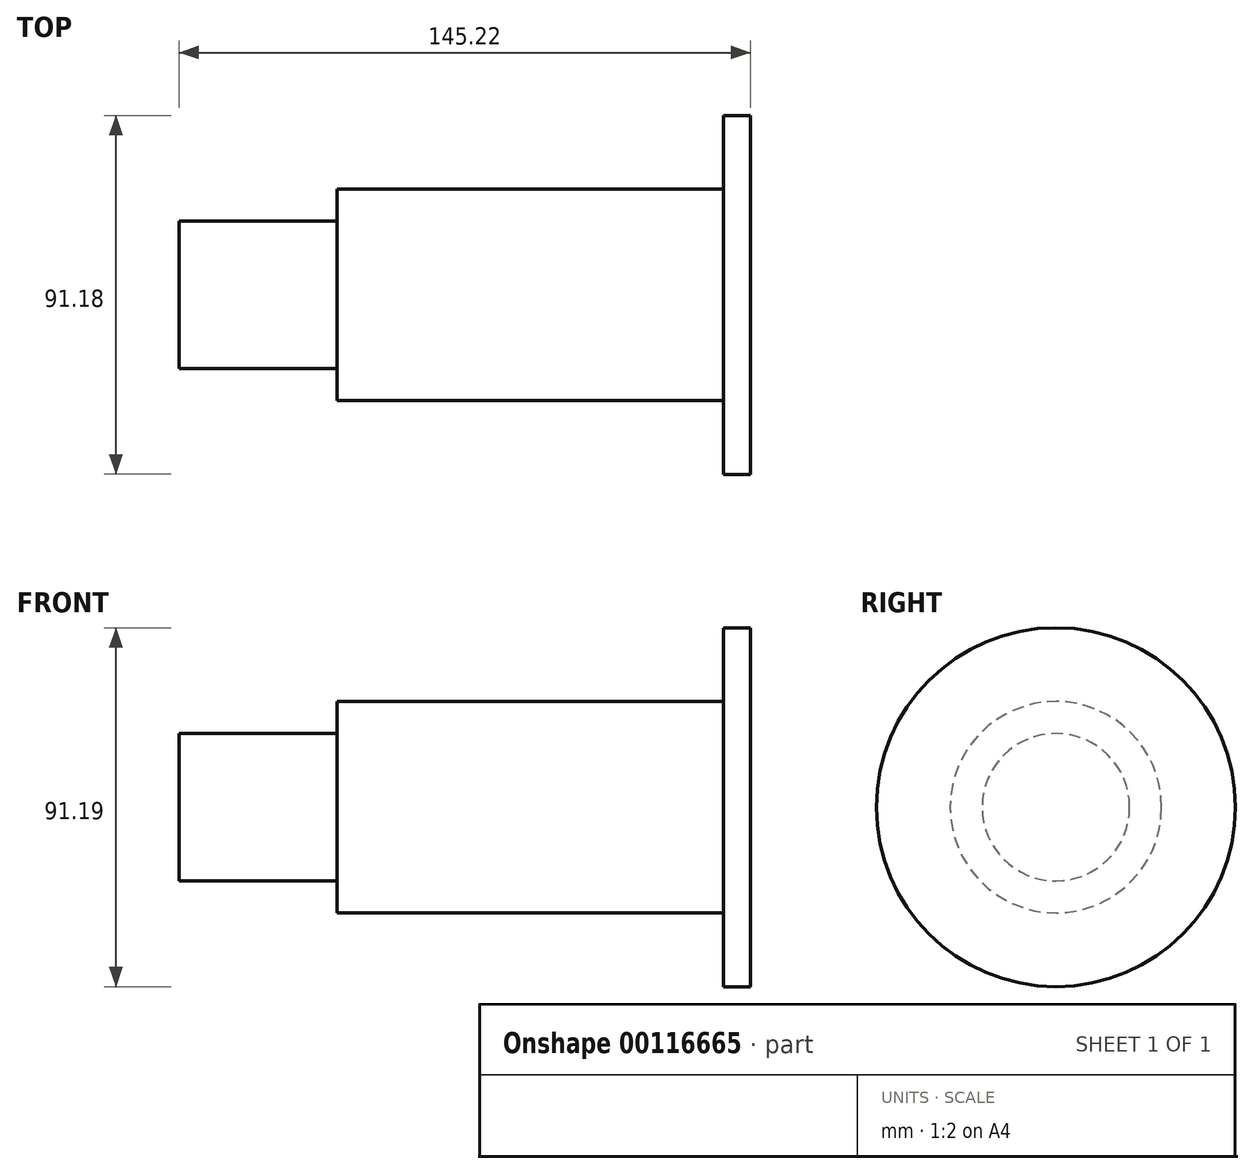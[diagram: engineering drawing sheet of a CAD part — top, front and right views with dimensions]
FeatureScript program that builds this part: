
annotation { "Feature Type Name" : "Feature", "Feature Type Description" : "" }
export const myFeature = defineFeature(function(context is Context, id is Id, definition is map)
    precondition{}
    {
        {
            var Q0;
            Q0=qCreatedBy(makeId("Front.planeOp"),FACE);
            var sketch = newSketch(context, id + "F0", { "sketchPlane" : qUnion([Q0])});
            skLineSegment(sketch, "E0.bottom", {"start": v(-50.8, 4.06) * mm, "end": v(50.8, 4.06) * mm});
            skLineSegment(sketch, "E0.top", {"start": v(-50.8, -4.06) * mm, "end": v(50.8, -4.06) * mm});
            skLineSegment(sketch, "E0.left", {"start": v(-50.8, 4.06) * mm, "end": v(-50.8, -4.06) * mm});
            skLineSegment(sketch, "E0.right", {"start": v(50.8, 4.06) * mm, "end": v(50.8, -4.06) * mm});
            skPoint(sketch, "E0.middle", {"position": v(0, 0) * mm});
            skLineSegment(sketch, "E1.bottom", {"start": v(54.23, 22.8) * mm, "end": v(47.37, 22.8) * mm});
            skLineSegment(sketch, "E1.top", {"start": v(54.23, -22.8) * mm, "end": v(47.37, -22.8) * mm});
            skLineSegment(sketch, "E1.left", {"start": v(54.23, 22.8) * mm, "end": v(54.23, -22.8) * mm});
            skLineSegment(sketch, "E1.right", {"start": v(47.37, 22.8) * mm, "end": v(47.37, -22.8) * mm});
            skPoint(sketch, "E1.middle", {"position": v(50.8, 0) * mm});
            skSolve(sketch);
        }
        {
            var Q0;
            {var subQ1=sQuery(id+"F0.wireOp",EDGE,"E0.right");Q0=makeQuery(id+"F0.imprint","IMPRINT",FACE,{"disambiguationData":[TD([[makeQuery(id+"F0.imprint","IMPRINT",EDGE,{"derivedFrom":subQ1}),1.0]])]});}
            var Q1;
            {var subQ0=sQuery(id+"F0.wireOp",EDGE,"E0.right");Q1=makeQuery(id+"F0.imprint","IMPRINT",FACE,{"disambiguationData":[TD([[makeQuery(id+"F0.imprint","IMPRINT",EDGE,{"derivedFrom":subQ0}),-1.0]])]});}
            var Q2;
            {var subQ0=sQuery(id+"F0.wireOp",EDGE,"E0.left");Q2=makeQuery(id+"F0.imprint","IMPRINT",FACE,{"disambiguationData":[TD([[makeQuery(id+"F0.imprint","IMPRINT",EDGE,{"derivedFrom":subQ0}),1.0]])]});}
            var Q3;
            Q3=sQuery(id+"F0.wireOp",EDGE,"E1.bottom");
            revolve(context, id + "F1", {"entities" : qUnion([Q0, Q1, Q2]), "axis" : qUnion([Q3]), "revolveType" : RevolveType.FULL});
        }
        {
            var Q0;
            {var subQ0=sQuery(id+"F0.wireOp",EDGE,"E1.right");Q0=makeQuery(id+"F1.opRevolve","SWEPT_FACE",FACE,{"disambiguationData":[OSD([subQ0]),TDD([makeQuery(id+"F0.imprint","IMPRINT",EDGE,{"disambiguationData":[TD([[makeQuery(id+"F0.imprint","INTERSECT",VERTEX,{"derivedFrom":[sQuery(id+"F0.wireOp",EDGE,"E1.bottom"),subQ0]}),-1.0]])],"derivedFrom":subQ0})])]});}
            extrude(context, id + "F2", {"entities" : qUnion([Q0]), "operationType" : NewBodyOperationType.ADD, "depth" : 138.35 * mm});
        }
    });
